# Revit family: Zaniboni-Bongo-3_Inch_Adj_Pendant-1
name_source: partatom
category: Lighting Fixtures
revit_build: Autodesk Revit 2016 (Build: 20150220_1215(x64)
units: mm (PartAtom-declared; Revit-internal decimal feet)

## family parameters
Cut with Voids When Loaded = No
Host = Face
Light Source = Yes
Part Type = Normal
Room Calculation Point = No
Round Connector Dimension = Use Diameter
Shared = No

## types (1)
- P2-BON3PO-1327A-2C-WS
    Assembly Code = E1020300
    Beam = 24°
    Body Finish = ZBN - Metal Matte Black
    CRI = 80
    Color Filter = 16777215
    Default Elevation = 48"
    Description = 4 inch Round Adjustable 20°
    Diameter = 4 1/64"
    Dimming Lamp Color Temperature Shift = <None>
    Emit Shape Visible in Rendering = No
    Emit from Circle Diameter = 4"
    Frame Finish = ZBN - Metal Matte Black
    Kelvin = 2700K
    Keynote = 12500
    Manufacturer = Zaniboni
    Mechanism Finish = ZBN - Metal Matte Black
    Model = P2-BON3PO-1327A-2C-WS
    Photometric Web File = generic
    Screen Finish = ZBN - Glass
    Support Finish = ZBN - Metal Matte Black
    Tilt Angle = 20.00°
    Type Comments = Bongo
    URL = www.zanibonilighting.com
    Voltage = 120 V
    Wattage Comments = 7W
    Wire Finish = ZBN - Metal Matte Black

## geometry (parser evidence)
native form markers: Blend x2, Sweep x3
no freeform markers — native parametric forms only
